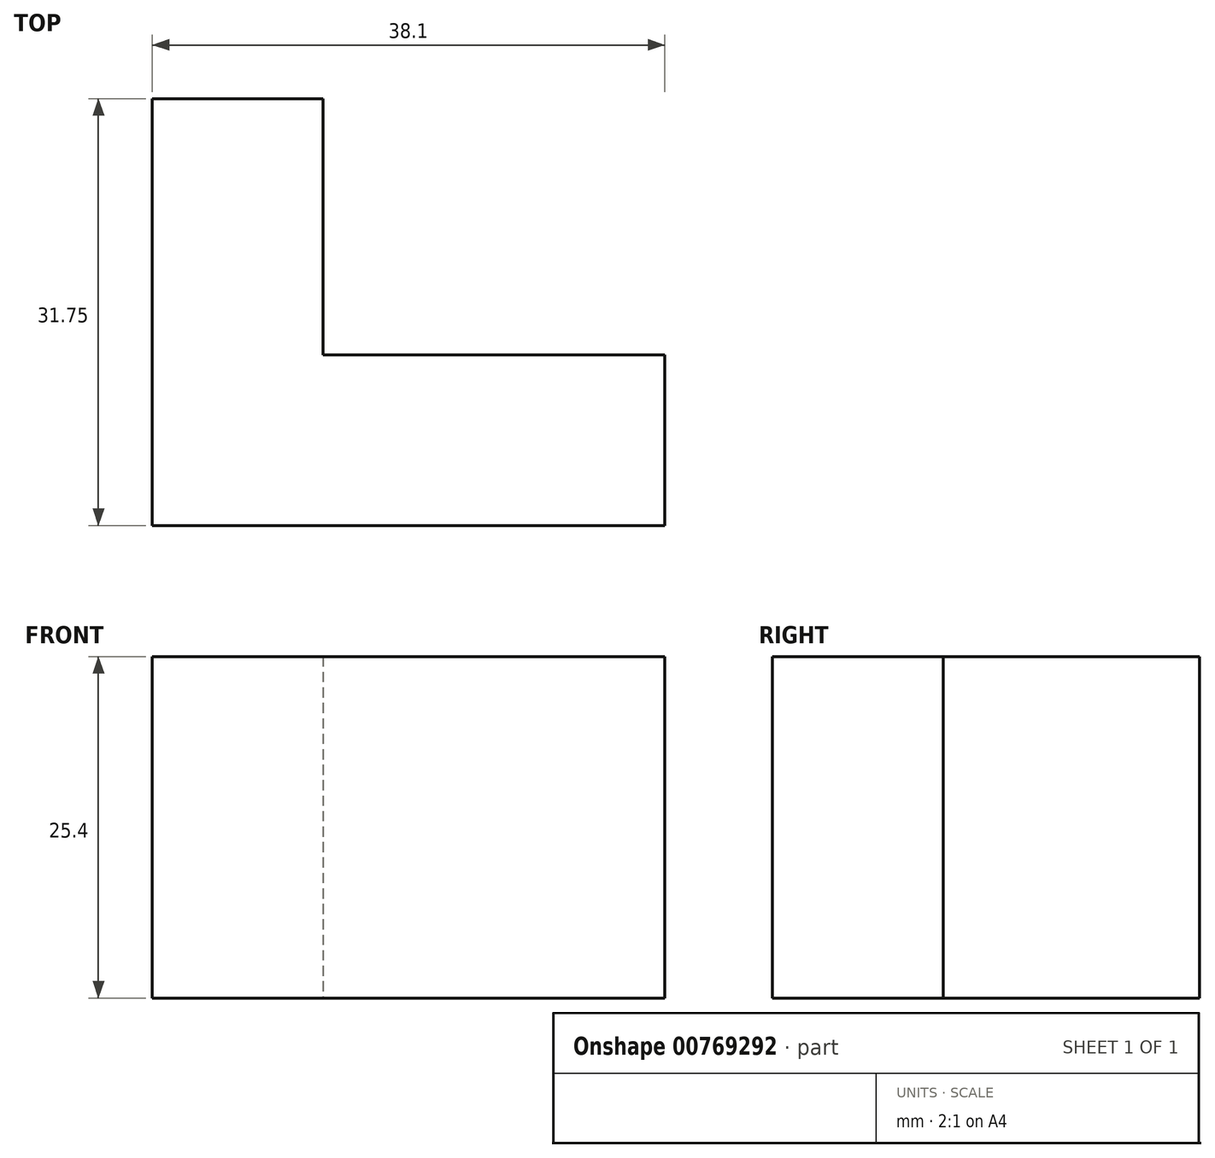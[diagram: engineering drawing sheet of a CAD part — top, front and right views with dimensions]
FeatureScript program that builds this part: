
annotation { "Feature Type Name" : "Feature", "Feature Type Description" : "" }
export const myFeature = defineFeature(function(context is Context, id is Id, definition is map)
    precondition{}
    {
        {
            var Q0;
            Q0=qCreatedBy(makeId("Top.planeOp"),FACE);
            var sketch = newSketch(context, id + "F0", { "sketchPlane" : qUnion([Q0])});
            skLineSegment(sketch, "E0", {"start": v(0, 0) * mm, "end": v(38.1, 0) * mm});
            skLineSegment(sketch, "E1", {"start": v(0, 0) * mm, "end": v(0, 31.75) * mm});
            skLineSegment(sketch, "E2", {"start": v(0, 31.75) * mm, "end": v(12.7, 31.75) * mm});
            skLineSegment(sketch, "E3", {"start": v(12.7, 31.75) * mm, "end": v(12.7, 12.7) * mm});
            skLineSegment(sketch, "E4", {"start": v(12.7, 12.7) * mm, "end": v(38.1, 12.7) * mm});
            skLineSegment(sketch, "E5", {"start": v(38.1, 12.7) * mm, "end": v(38.1, 0) * mm});
            skSolve(sketch);
        }
        {
            var Q0;
            Q0=makeQuery(id+"F0.imprint","IMPRINT",FACE,{"disambiguationData":[TD([[makeQuery(id+"F0.imprint","IMPRINT",EDGE,{"derivedFrom":sQuery(id+"F0.wireOp",EDGE,"E0")}),1.0]])]});
            extrude(context, id + "F1", {"entities" : qUnion([Q0]), "depth" : 25.4 * mm, "offsetDistance" : 25.4 * mm});
        }
    });
